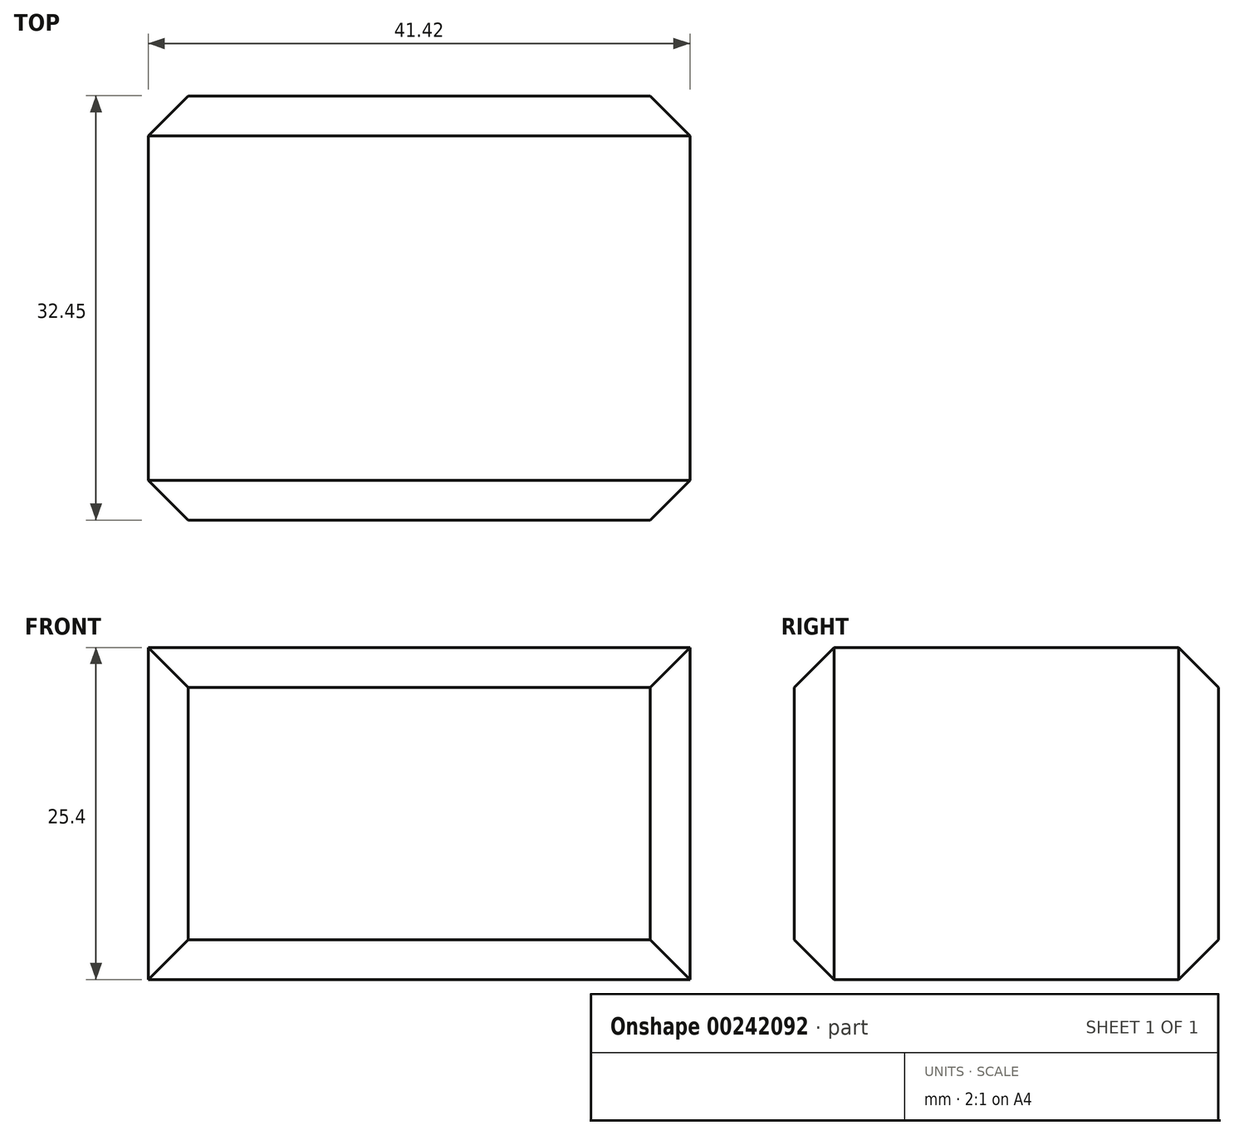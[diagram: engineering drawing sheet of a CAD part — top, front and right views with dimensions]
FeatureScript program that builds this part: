
annotation { "Feature Type Name" : "Feature", "Feature Type Description" : "" }
export const myFeature = defineFeature(function(context is Context, id is Id, definition is map)
    precondition{}
    {
        {
            var Q0;
            Q0=qCreatedBy(makeId("Top.planeOp"),FACE);
            var sketch = newSketch(context, id + "F0", { "sketchPlane" : qUnion([Q0])});
            skLineSegment(sketch, "E0.bottom", {"start": v(3.77, -8.8) * mm, "end": v(-37.65, -8.8) * mm});
            skLineSegment(sketch, "E0.top", {"start": v(3.77, 23.65) * mm, "end": v(-37.65, 23.65) * mm});
            skLineSegment(sketch, "E0.left", {"start": v(3.77, -8.8) * mm, "end": v(3.77, 23.65) * mm});
            skLineSegment(sketch, "E0.right", {"start": v(-37.65, -8.8) * mm, "end": v(-37.65, 23.65) * mm});
            skSolve(sketch);
        }
        {
            var Q0;
            Q0 = qSketchRegion(id + "F0", true);
            extrude(context, id + "F1", {"entities" : qUnion([Q0]), "depth" : 25.4 * mm});
        }
        {
            var Q0;
            Q0=makeQuery(id+"F1.opExtrude","SWEPT_FACE",FACE,{"disambiguationData":[OSD([sQuery(id+"F0.wireOp",EDGE,"E0.bottom")])]});
            var sketch = newSketch(context, id + "F2", { "sketchPlane" : qUnion([Q0])});
            skCircle(sketch, "E1", {"center": v(-16.94, 12.64) * mm, "radius": 7.88 * mm});
            skPoint(sketch, "E1.centerSnap0", {"position": v(-16.94, 25.4) * mm});
            skSolve(sketch);
        }
        {
            var Q0;
            Q0=sQuery(id+"F2.wireOp",EDGE,"E1");
            extrude(context, id + "F3", {"bodyType" : ToolBodyType.SURFACE, "surfaceEntities" : qUnion([Q0]), "depth" : 38.1 * mm});
        }
        {
            var Q0;
            Q0=makeQuery(id+"F1.opExtrude","SWEPT_FACE",FACE,{"disambiguationData":[OSD([sQuery(id+"F0.wireOp",EDGE,"E0.top")])]});
            var Q1;
            Q1=makeQuery(id+"F1.opExtrude","SWEPT_FACE",FACE,{"disambiguationData":[OSD([sQuery(id+"F0.wireOp",EDGE,"E0.bottom")])]});
            chamfer(context, id + "F4", {"entities" : qUnion([Q0, Q1]), "width" : 3.05 * mm, "tangentPropagation" : true});
        }
    });
